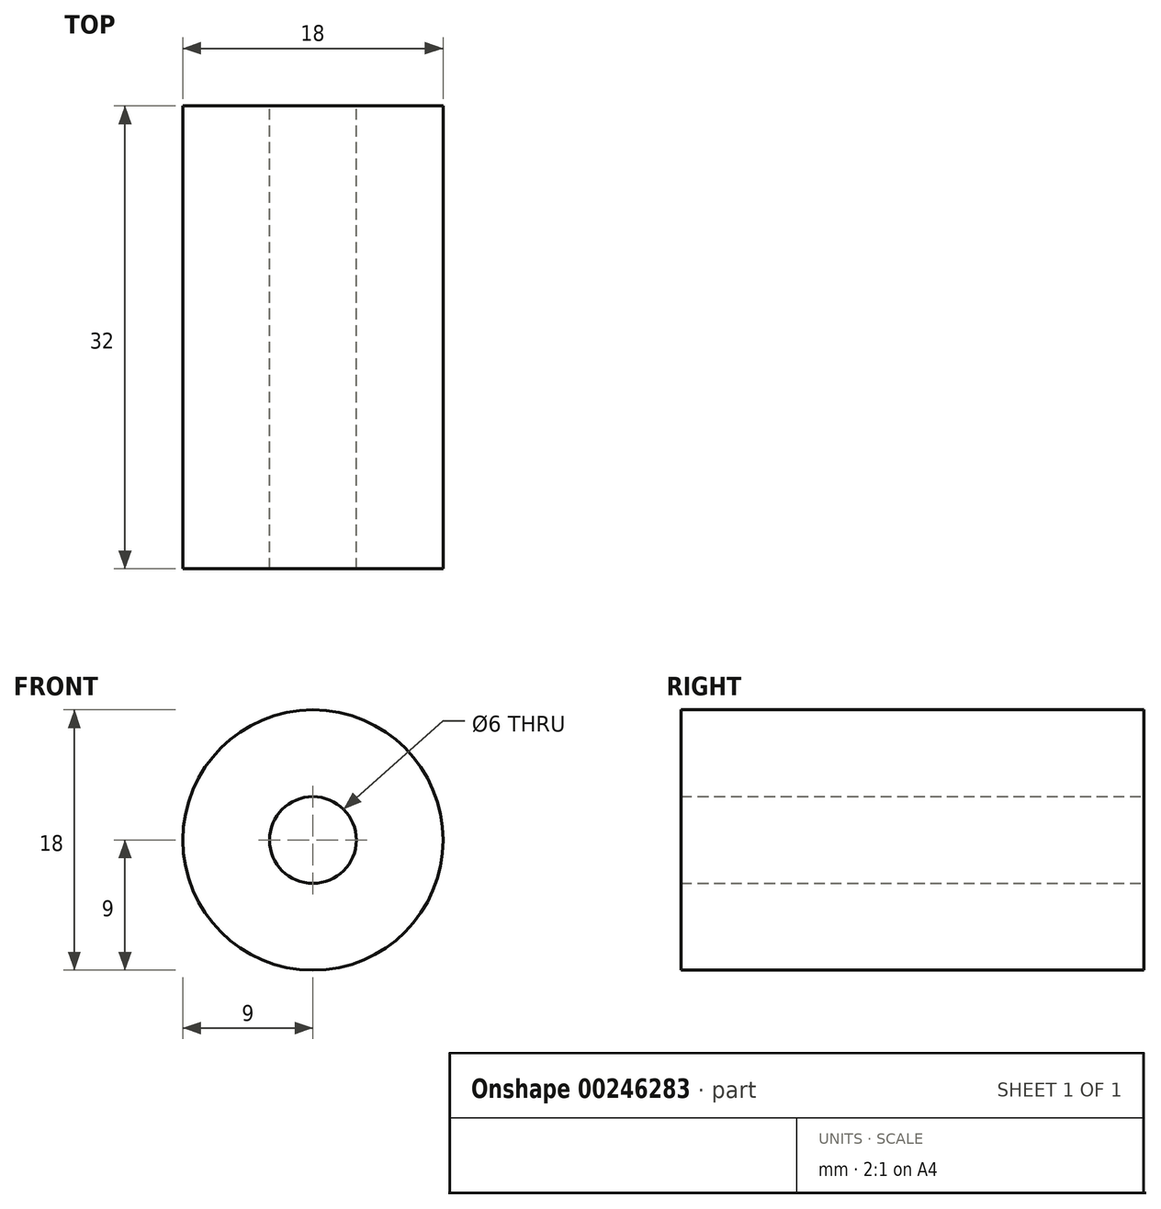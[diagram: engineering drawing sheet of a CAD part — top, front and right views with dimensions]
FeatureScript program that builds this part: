
annotation { "Feature Type Name" : "Feature", "Feature Type Description" : "" }
export const myFeature = defineFeature(function(context is Context, id is Id, definition is map)
    precondition{}
    {
        {
            var Q0;
            Q0=qCreatedBy(makeId("Front.planeOp"),FACE);
            var sketch = newSketch(context, id + "F0", { "sketchPlane" : qUnion([Q0])});
            skCircle(sketch, "E0", {"center": v(0, 0) * mm, "radius": 9 * mm});
            skCircle(sketch, "E1", {"center": v(0, 0) * mm, "radius": 3 * mm});
            skSolve(sketch);
        }
        {
            var Q0;
            Q0 = qSketchRegion(id + "F0", true);
            extrude(context, id + "F1", {"entities" : qUnion([Q0]), "depth" : 32 * mm});
        }
    });
